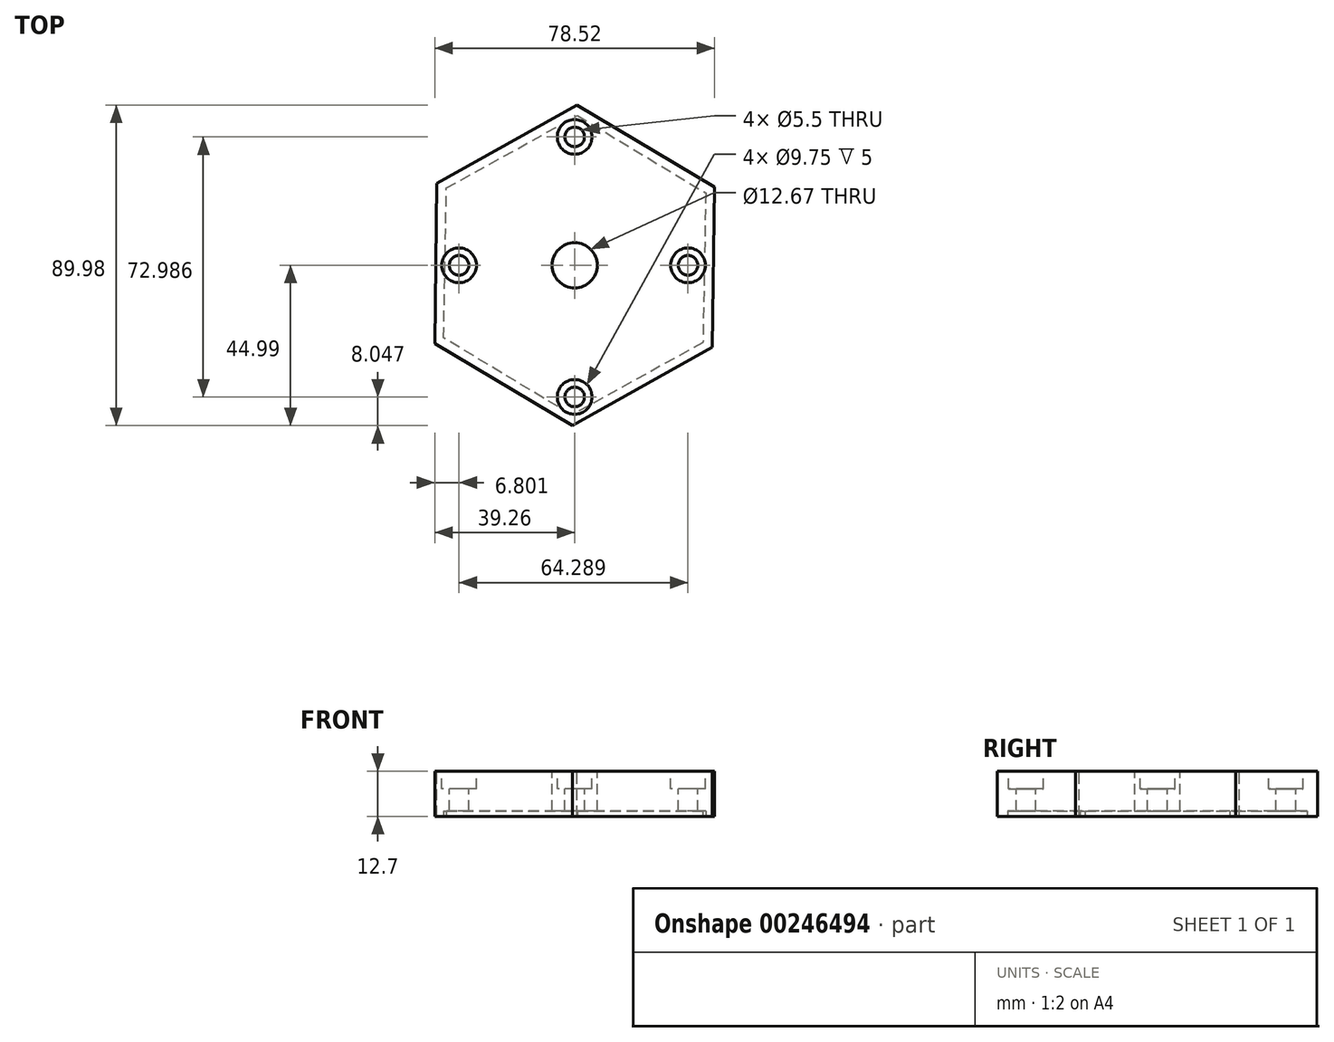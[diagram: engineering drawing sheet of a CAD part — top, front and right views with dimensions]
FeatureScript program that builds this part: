
annotation { "Feature Type Name" : "Feature", "Feature Type Description" : "" }
export const myFeature = defineFeature(function(context is Context, id is Id, definition is map)
    precondition{}
    {
        {
            var Q0;
            Q0=qCreatedBy(makeId("Top.planeOp"),FACE);
            var sketch = newSketch(context, id + "F0", { "sketchPlane" : qUnion([Q0])});
            skCircle(sketch, "E0.cCircle", {"center": v(0, 0) * mm, "radius": 38.97 * mm, "construction": true});
            skLineSegment(sketch, "E0.0", {"start": v(38.67, -23) * mm, "end": v(-0.58, -45) * mm});
            skLineSegment(sketch, "E0.1", {"start": v(-0.58, -45) * mm, "end": v(-39.26, -22) * mm});
            skLineSegment(sketch, "E0.2", {"start": v(-39.26, -22) * mm, "end": v(-38.67, 23) * mm});
            skLineSegment(sketch, "E0.3", {"start": v(-38.67, 23) * mm, "end": v(0.58, 45) * mm});
            skLineSegment(sketch, "E0.4", {"start": v(0.58, 45) * mm, "end": v(39.26, 22) * mm});
            skLineSegment(sketch, "E0.5", {"start": v(39.26, 22) * mm, "end": v(38.67, -23) * mm});
            skPoint(sketch, "E0.0.midPoint", {"position": v(19.04, -34) * mm});
            skSolve(sketch);
        }
        {
            var Q0;
            Q0 = qSketchRegion(id + "F0", true);
            extrude(context, id + "F1", {"entities" : qUnion([Q0]), "oppositeDirection" : true, "depth" : 12.7 * mm});
        }
        {
            var Q0;
            Q0=qCreatedBy(makeId("Top.planeOp"),FACE);
            var sketch = newSketch(context, id + "F2", { "sketchPlane" : qUnion([Q0])});
            skCircle(sketch, "E1", {"center": v(0, 36.04) * mm, "radius": 3.25 * mm});
            skCircle(sketch, "E2", {"center": v(-32.46, 0) * mm, "radius": 3.22 * mm});
            skCircle(sketch, "E3", {"center": v(31.83, 0) * mm, "radius": 3.29 * mm});
            skCircle(sketch, "E4", {"center": v(0, -36.94) * mm, "radius": 3.32 * mm});
            skSolve(sketch);
        }
        {
            var Q0;
            Q0=sQuery(id+"F2.wireOp",VERTEX,"E4.center");
            var Q1;
            Q1=sQuery(id+"F2.wireOp",VERTEX,"E3.center");
            var Q2;
            Q2=sQuery(id+"F2.wireOp",VERTEX,"E1.center");
            var Q3;
            Q3=sQuery(id+"F2.wireOp",VERTEX,"E2.center");
            var Q4;
            Q4=makeQuery(id+"F1.opExtrude","SWEPT_BODY",BODY,{"disambiguationData":[OSD([sQuery(id+"F0.wireOp",EDGE,"E0.0"),sQuery(id+"F0.wireOp",EDGE,"E0.1"),sQuery(id+"F0.wireOp",EDGE,"E0.2"),sQuery(id+"F0.wireOp",EDGE,"E0.3"),sQuery(id+"F0.wireOp",EDGE,"E0.4"),sQuery(id+"F0.wireOp",EDGE,"E0.5")])]});
            hole(context, id + "F3", {"style" : HoleStyle.C_BORE, "endStyle" : HoleEndStyle.THROUGH, "holeDiameter" : 5.5 * mm, "cBoreDiameter" : 9.75 * mm, "cBoreDepth" : 5 * mm, "tappedDepth" : 12.7 * mm, "tapClearance" : 3, "startFromSketch" : true, "locations" : qUnion([Q0, Q1, Q2, Q3]), "scope" : qUnion([Q4])});
        }
        {
            var Q0;
            Q0=qCreatedBy(makeId("Top.planeOp"),FACE);
            var sketch = newSketch(context, id + "F4", { "sketchPlane" : qUnion([Q0])});
            skCircle(sketch, "E5", {"center": v(0, 0) * mm, "radius": 6.34 * mm});
            skSolve(sketch);
        }
        {
            var Q0;
            Q0 = qSketchRegion(id + "F4", true);
            extrude(context, id + "F5", {"entities" : qUnion([Q0]), "operationType" : NewBodyOperationType.REMOVE, "oppositeDirection" : true, "depth" : 25.4 * mm});
        }
        {
            var Q0;
            Q0=qCreatedBy(makeId("Top.planeOp"),FACE);
            cPlane(context, id + "F6", {"entities" : qUnion([Q0]), "cplaneType" : CPlaneType.OFFSET, "offset" : 12.7 * mm, "oppositeDirection" : true, "width" : 152.4 * mm, "height" : 152.4 * mm});
        }
        {
            var Q0;
            Q0=qCreatedBy(id+"F6.planeOp",FACE);
            var sketch = newSketch(context, id + "F7", { "sketchPlane" : qUnion([Q0])});
            skCircle(sketch, "E6.cCircle", {"center": v(0, 0) * mm, "radius": 36.4 * mm, "construction": true});
            skLineSegment(sketch, "E6.0", {"start": v(0.78, 42.03) * mm, "end": v(36.8, 20.34) * mm});
            skLineSegment(sketch, "E6.1", {"start": v(36.8, 20.34) * mm, "end": v(36.01, -21.7) * mm});
            skLineSegment(sketch, "E6.2", {"start": v(36.01, -21.7) * mm, "end": v(-0.78, -42.03) * mm});
            skLineSegment(sketch, "E6.3", {"start": v(-0.78, -42.03) * mm, "end": v(-36.8, -20.34) * mm});
            skLineSegment(sketch, "E6.4", {"start": v(-36.8, -20.34) * mm, "end": v(-36.01, 21.7) * mm});
            skLineSegment(sketch, "E6.5", {"start": v(-36.01, 21.7) * mm, "end": v(0.78, 42.03) * mm});
            skPoint(sketch, "E6.0.midPoint", {"position": v(18.79, 31.19) * mm});
            skSolve(sketch);
        }
        {
            var Q0;
            Q0=makeQuery(id+"F7.imprint","IMPRINT",FACE,{"disambiguationData":[TD([[makeQuery(id+"F7.imprint","IMPRINT",EDGE,{"derivedFrom":sQuery(id+"F7.wireOp",EDGE,"E6.0")}),-1.0]])]});
            extrude(context, id + "F8", {"entities" : qUnion([Q0]), "operationType" : NewBodyOperationType.REMOVE, "depth" : 1.59 * mm});
        }
    });
